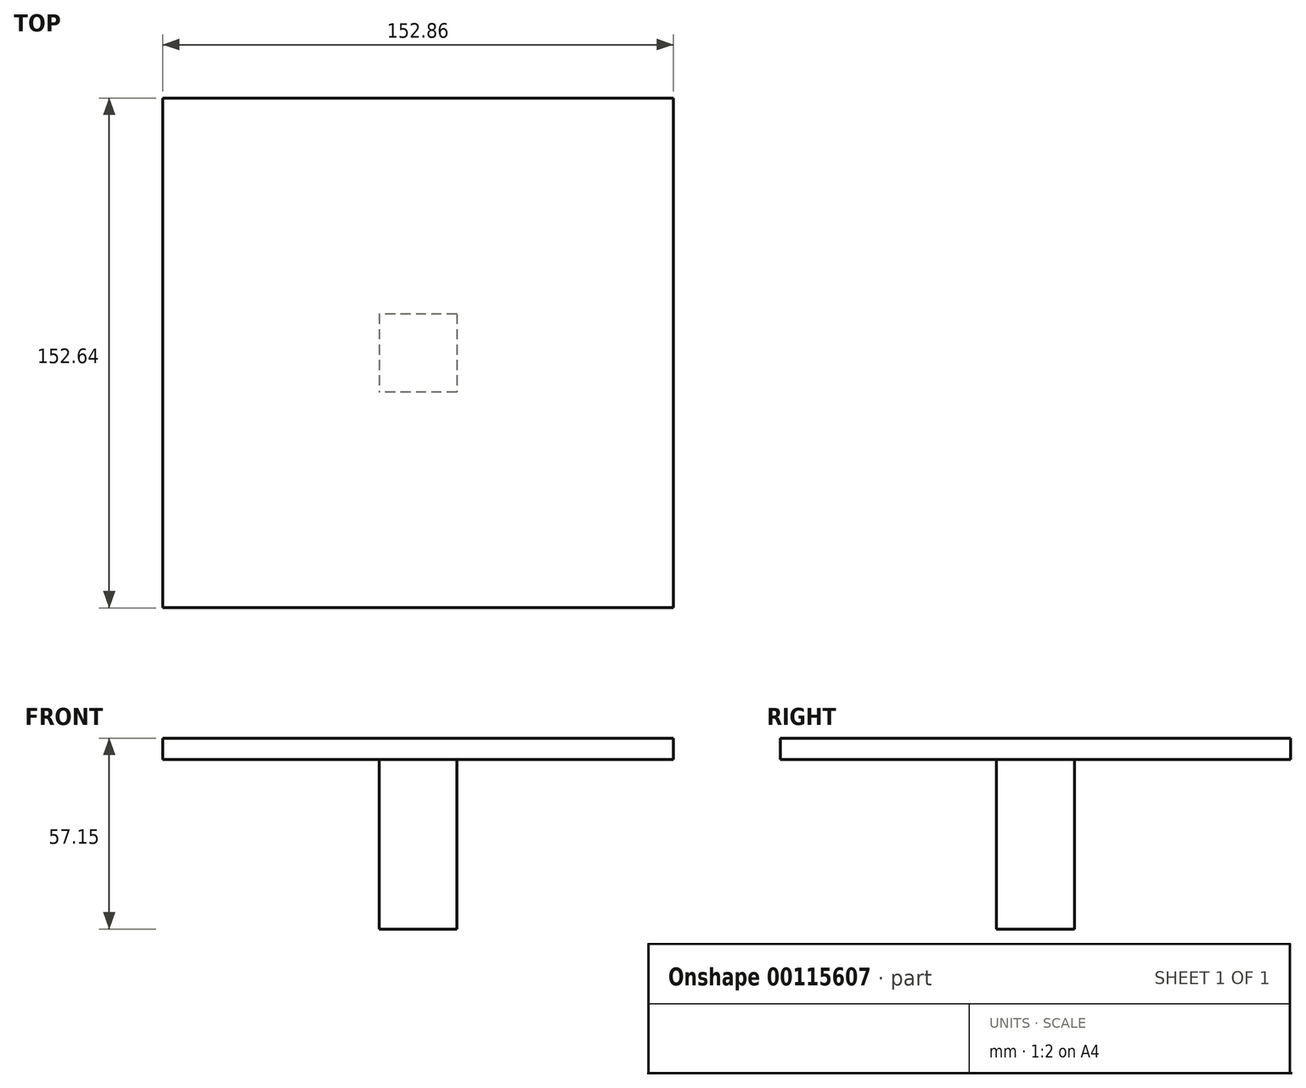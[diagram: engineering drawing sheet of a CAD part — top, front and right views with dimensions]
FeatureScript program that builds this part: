
annotation { "Feature Type Name" : "Feature", "Feature Type Description" : "" }
export const myFeature = defineFeature(function(context is Context, id is Id, definition is map)
    precondition{}
    {
        {
            var Q0;
            Q0=qCreatedBy(makeId("Top.planeOp"),FACE);
            var sketch = newSketch(context, id + "F0", { "sketchPlane" : qUnion([Q0])});
            skLineSegment(sketch, "E0.bottom", {"start": v(76.43, -76.32) * mm, "end": v(-76.43, -76.32) * mm});
            skLineSegment(sketch, "E0.top", {"start": v(76.43, 76.32) * mm, "end": v(-76.43, 76.32) * mm});
            skLineSegment(sketch, "E0.left", {"start": v(76.43, -76.32) * mm, "end": v(76.43, 76.32) * mm});
            skLineSegment(sketch, "E0.right", {"start": v(-76.43, -76.32) * mm, "end": v(-76.43, 76.32) * mm});
            skPoint(sketch, "E0.middle", {"position": v(0, 0) * mm});
            skSolve(sketch);
        }
        {
            var Q0;
            Q0=makeQuery(id+"F0.imprint","IMPRINT",FACE,{"disambiguationData":[TD([[makeQuery(id+"F0.imprint","IMPRINT",EDGE,{"derivedFrom":sQuery(id+"F0.wireOp",EDGE,"E0.bottom")}),-1.0]])]});
            extrude(context, id + "F1", {"entities" : qUnion([Q0]), "depth" : 6.35 * mm});
        }
        {
            var Q0;
            Q0=makeQuery(id+"F1.opExtrude","CAP_FACE",FACE,{"disambiguationData":[OSD([sQuery(id+"F0.wireOp",EDGE,"E0.bottom"),sQuery(id+"F0.wireOp",EDGE,"E0.top"),sQuery(id+"F0.wireOp",EDGE,"E0.left"),sQuery(id+"F0.wireOp",EDGE,"E0.right")])],"isStart":true});
            var sketch = newSketch(context, id + "F2", { "sketchPlane" : qUnion([Q0])});
            skLineSegment(sketch, "E1.bottom", {"start": v(13.29, 13.32) * mm, "end": v(-13.29, 13.32) * mm});
            skLineSegment(sketch, "E1.top", {"start": v(13.29, -13.32) * mm, "end": v(-13.29, -13.32) * mm});
            skLineSegment(sketch, "E1.left", {"start": v(13.29, 13.32) * mm, "end": v(13.29, -13.32) * mm});
            skLineSegment(sketch, "E1.right", {"start": v(-13.29, 13.32) * mm, "end": v(-13.29, -13.32) * mm});
            skPoint(sketch, "E1.middle", {"position": v(0, 0) * mm});
            skSolve(sketch);
        }
        {
            var Q0;
            Q0 = qConstructionFilter(qBodyType(qCreatedBy(id + "F2" ,EDGE), BodyType.WIRE), ConstructionObject.NO);
            var Q1;
            Q1=sQuery(id+"F2.wireOp",EDGE,"E1.right");
            extrude(context, id + "F3", {"bodyType" : ToolBodyType.SURFACE, "surfaceEntities" : qUnion([Q0, Q1]), "depth" : 76.2 * mm});
        }
        {
            var Q0;
            Q0=makeQuery(id+"F1.opExtrude","CAP_FACE",FACE,{"disambiguationData":[OSD([sQuery(id+"F0.wireOp",EDGE,"E0.bottom"),sQuery(id+"F0.wireOp",EDGE,"E0.top"),sQuery(id+"F0.wireOp",EDGE,"E0.left"),sQuery(id+"F0.wireOp",EDGE,"E0.right")])],"isStart":true});
            var sketch = newSketch(context, id + "F4", { "sketchPlane" : qUnion([Q0])});
            skLineSegment(sketch, "E2.bottom", {"start": v(11.56, -11.68) * mm, "end": v(-11.56, -11.68) * mm});
            skLineSegment(sketch, "E2.top", {"start": v(11.56, 11.68) * mm, "end": v(-11.56, 11.68) * mm});
            skLineSegment(sketch, "E2.left", {"start": v(11.56, -11.68) * mm, "end": v(11.56, 11.68) * mm});
            skLineSegment(sketch, "E2.right", {"start": v(-11.56, -11.68) * mm, "end": v(-11.56, 11.68) * mm});
            skPoint(sketch, "E2.middle", {"position": v(0, 0) * mm});
            skSolve(sketch);
        }
        {
            var Q0;
            Q0 = qSketchRegion(id + "F4", true);
            extrude(context, id + "F5", {"entities" : qUnion([Q0]), "operationType" : NewBodyOperationType.ADD, "depth" : 50.8 * mm});
        }
    });
